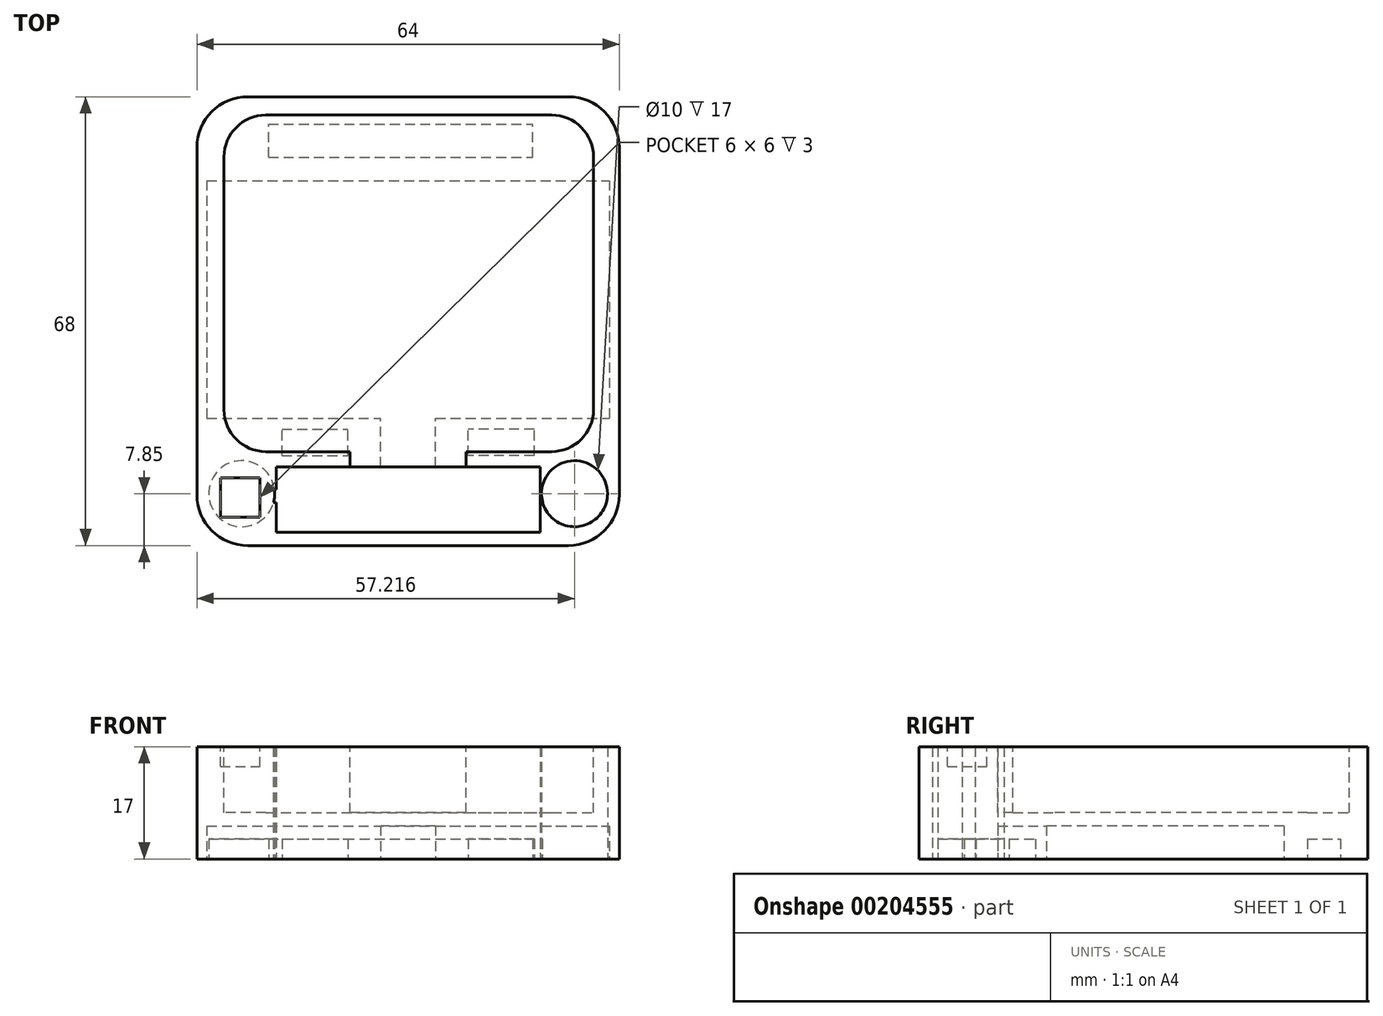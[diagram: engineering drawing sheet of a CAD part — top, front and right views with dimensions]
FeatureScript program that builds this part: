
annotation { "Feature Type Name" : "Feature", "Feature Type Description" : "" }
export const myFeature = defineFeature(function(context is Context, id is Id, definition is map)
    precondition{}
    {
        {
            var Q0;
            Q0=qCreatedBy(makeId("Top.planeOp"),FACE);
            var sketch = newSketch(context, id + "F0", { "sketchPlane" : qUnion([Q0])});
            skLineSegment(sketch, "E0.bottom", {"start": v(-24.3, 34) * mm, "end": v(24.3, 34) * mm});
            skLineSegment(sketch, "E0.top", {"start": v(-24.3, -34) * mm, "end": v(24.3, -34) * mm});
            skLineSegment(sketch, "E0.left", {"start": v(-32, 26.3) * mm, "end": v(-32, -26.3) * mm});
            skLineSegment(sketch, "E0.right", {"start": v(32, 26.3) * mm, "end": v(32, -26.3) * mm});
            skPoint(sketch, "E0.middle", {"position": v(0, 0) * mm});
            skPoint(sketch, "E1.visualSharp", {"position": v(32, 34) * mm});
            skArc(sketch, "E1.filletArc", {"start": v(32, 26.3) * mm, "mid": v(29.75, 31.75) * mm, "end": v(24.3, 34) * mm});
            skPoint(sketch, "E2.visualSharp", {"position": v(-32, 34) * mm});
            skArc(sketch, "E2.filletArc", {"start": v(-24.3, 34) * mm, "mid": v(-29.75, 31.75) * mm, "end": v(-32, 26.3) * mm});
            skPoint(sketch, "E3.visualSharp", {"position": v(-32, -34) * mm});
            skArc(sketch, "E3.filletArc", {"start": v(-32, -26.3) * mm, "mid": v(-29.75, -31.75) * mm, "end": v(-24.3, -34) * mm});
            skPoint(sketch, "E4.visualSharp", {"position": v(32, -34) * mm});
            skArc(sketch, "E4.filletArc", {"start": v(24.3, -34) * mm, "mid": v(29.75, -31.75) * mm, "end": v(32, -26.3) * mm});
            skLineSegment(sketch, "E5", {"start": v(0, -34) * mm, "end": v(0, -32) * mm});
            skPoint(sketch, "E5.endSnap0", {"position": v(0, -34) * mm});
            skLineSegment(sketch, "E6.bottom", {"start": v(0, -32) * mm, "end": v(-20, -32) * mm});
            skLineSegment(sketch, "E6.top", {"start": v(0, -22.07) * mm, "end": v(-20, -22.07) * mm});
            skLineSegment(sketch, "E6.left", {"start": v(0, -32) * mm, "end": v(0, -22.07) * mm});
            skLineSegment(sketch, "E6.right", {"start": v(-20, -32) * mm, "end": v(-20, -22.07) * mm});
            skLineSegment(sketch, "E7.bottom", {"start": v(0, -32) * mm, "end": v(20, -32) * mm});
            skLineSegment(sketch, "E7.top", {"start": v(0, -22.07) * mm, "end": v(20, -22.07) * mm});
            skLineSegment(sketch, "E7.right", {"start": v(20, -32) * mm, "end": v(20, -22.07) * mm});
            skCircle(sketch, "E8", {"center": v(-25.22, -26.15) * mm, "radius": 5 * mm});
            skCircle(sketch, "E9.MirrorC", {"center": v(25.22, -26.15) * mm, "radius": 5 * mm});
            skLineSegment(sketch, "E10.MirrorCS", {"start": v(30.68, -30.61) * mm, "end": v(28.93, -29.65) * mm});
            skLineSegment(sketch, "E11.bottom", {"start": v(-30.5, 21.3) * mm, "end": v(30.5, 21.3) * mm});
            skLineSegment(sketch, "E11.top", {"start": v(-30.5, -14.7) * mm, "end": v(30.5, -14.7) * mm});
            skLineSegment(sketch, "E11.left", {"start": v(-30.5, 21.3) * mm, "end": v(-30.5, -14.7) * mm});
            skLineSegment(sketch, "E11.right", {"start": v(30.5, 21.3) * mm, "end": v(30.5, -14.7) * mm});
            skLineSegment(sketch, "E12", {"start": v(-32, 15.13) * mm, "end": v(-30.5, 15.13) * mm});
            skLineSegment(sketch, "E13", {"start": v(30.5, 14.25) * mm, "end": v(32, 14.25) * mm});
            skLineSegment(sketch, "E14", {"start": v(-20.26, -25.53) * mm, "end": v(-20, -25.53) * mm});
            skLineSegment(sketch, "E15", {"start": v(-20, -25.53) * mm, "end": v(-20, -27.49) * mm});
            skLineSegment(sketch, "E16", {"start": v(-20, -27.49) * mm, "end": v(-20.4, -27.49) * mm});
            skLineSegment(sketch, "E17", {"start": v(20, -25.4) * mm, "end": v(20.27, -25.4) * mm});
            skLineSegment(sketch, "E18", {"start": v(20, -27.17) * mm, "end": v(20.32, -27.17) * mm});
            skLineSegment(sketch, "E19", {"start": v(-4.15, -22.07) * mm, "end": v(-4.15, -14.7) * mm});
            skLineSegment(sketch, "E20.MirrorCS", {"start": v(4.15, -22.07) * mm, "end": v(4.15, -14.7) * mm});
            skSolve(sketch);
        }
        {
            var Q0;
            Q0=makeQuery(id+"F0.imprint","IMPRINT",FACE,{"disambiguationData":[TD([[makeQuery(id+"F0.imprint","IMPRINT",EDGE,{"derivedFrom":sQuery(id+"F0.wireOp",EDGE,"E0.bottom")}),-1.0]])]});
            var Q1;
            {var subQ5=sQuery(id+"F0.wireOp",EDGE,"fJw1VMtN-DNDU-9MxT-oK31-EzQkojQoViIx.bottom");Q1=makeQuery(id+"F0.imprint","IMPRINT",FACE,{"disambiguationData":[TD([[makeQuery(id+"F0.imprint","IMPRINT",EDGE,{"derivedFrom":subQ5}),-1.0]])]});}
            var Q2;
            {var subQ14=sQuery(id+"F0.wireOp",EDGE,"E3.filletArc");Q2=makeQuery(id+"F0.imprint","IMPRINT",FACE,{"disambiguationData":[TD([[makeQuery(id+"F0.imprint","IMPRINT",EDGE,{"derivedFrom":subQ14}),1.0]])]});}
            var Q3;
            {var subQ0=sQuery(id+"F0.wireOp",EDGE,"E5");Q3=makeQuery(id+"F0.imprint","IMPRINT",FACE,{"disambiguationData":[TD([[makeQuery(id+"F0.imprint","IMPRINT",EDGE,{"derivedFrom":subQ0}),-1.0]])]});}
            var Q4;
            {var subQ0=sQuery(id+"F0.wireOp",EDGE,"fJw1VMtN-DNDU-9MxT-oK31-EzQkojQoViIx.left");var subQ1=sQuery(id+"F0.wireOp",EDGE,"E11.bottom");var subQ2=makeQuery(id+"F0.imprint","INTERSECT",VERTEX,{"derivedFrom":[subQ1,subQ0]});Q4=makeQuery(id+"F0.imprint","IMPRINT",FACE,{"disambiguationData":[TD([[makeQuery(id+"F0.imprint","IMPRINT",EDGE,{"disambiguationData":[TD([[subQ2,-1.0]])],"derivedFrom":subQ1}),-1.0]])]});}
            var Q5;
            {var subQ0=sQuery(id+"F0.wireOp",EDGE,"E11.left");var subQ6=sQuery(id+"F0.wireOp",EDGE,"E11.bottom");var subQ7=makeQuery(id+"F0.imprint","INTERSECT",VERTEX,{"derivedFrom":[subQ6,subQ0]});Q5=makeQuery(id+"F0.imprint","IMPRINT",FACE,{"disambiguationData":[TD([[makeQuery(id+"F0.imprint","IMPRINT",EDGE,{"disambiguationData":[TD([[subQ7,-1.0]])],"derivedFrom":subQ6}),-1.0]])]});}
            var Q6;
            {var subQ0=sQuery(id+"F0.wireOp",EDGE,"E11.right");var subQ4=sQuery(id+"F0.wireOp",EDGE,"E11.bottom");var subQ5=makeQuery(id+"F0.imprint","INTERSECT",VERTEX,{"derivedFrom":[subQ4,subQ0]});Q6=makeQuery(id+"F0.imprint","IMPRINT",FACE,{"disambiguationData":[TD([[makeQuery(id+"F0.imprint","IMPRINT",EDGE,{"disambiguationData":[TD([[subQ5,1.0]])],"derivedFrom":subQ4}),-1.0]])]});}
            var Q7;
            {var subQ5=sQuery(id+"F0.wireOp",EDGE,"fJw1VMtN-DNDU-9MxT-oK31-EzQkojQoViIx.top");Q7=makeQuery(id+"F0.imprint","IMPRINT",FACE,{"disambiguationData":[TD([[makeQuery(id+"F0.imprint","IMPRINT",EDGE,{"derivedFrom":subQ5}),1.0]])]});}
            var Q8;
            {var subQ0=sQuery(id+"F0.wireOp",EDGE,"E19");Q8=makeQuery(id+"F0.imprint","IMPRINT",FACE,{"disambiguationData":[TD([[makeQuery(id+"F0.imprint","IMPRINT",EDGE,{"derivedFrom":subQ0}),-1.0]])]});}
            extrude(context, id + "F1", {"entities" : qUnion([Q0, Q1, Q2, Q3, Q4, Q5, Q6, Q7, Q8]), "depth" : 17 * mm});
        }
        {
            var Q0;
            {var subQ0=sQuery(id+"F0.wireOp",EDGE,"fJw1VMtN-DNDU-9MxT-oK31-EzQkojQoViIx.left");var subQ1=sQuery(id+"F0.wireOp",EDGE,"E11.bottom");var subQ2=makeQuery(id+"F0.imprint","INTERSECT",VERTEX,{"derivedFrom":[subQ1,subQ0]});Q0=makeQuery(id+"F0.imprint","IMPRINT",FACE,{"disambiguationData":[TD([[makeQuery(id+"F0.imprint","IMPRINT",EDGE,{"disambiguationData":[TD([[subQ2,-1.0]])],"derivedFrom":subQ1}),-1.0]])]});}
            var Q1;
            {var subQ0=sQuery(id+"F0.wireOp",EDGE,"E19");Q1=makeQuery(id+"F0.imprint","IMPRINT",FACE,{"disambiguationData":[TD([[makeQuery(id+"F0.imprint","IMPRINT",EDGE,{"derivedFrom":subQ0}),-1.0]])]});}
            extrude(context, id + "F2", {"entities" : qUnion([Q0, Q1]), "operationType" : NewBodyOperationType.REMOVE, "depth" : 5 * mm});
        }
        {
            var Q0;
            Q0=makeQuery(id+"F0.imprint","IMPRINT",FACE,{"disambiguationData":[TD([[makeQuery(id+"F0.imprint","IMPRINT",EDGE,{"derivedFrom":sQuery(id+"F0.wireOp",EDGE,"E8")}),1.0]])]});
            var Q1;
            {var subQ0=sQuery(id+"F0.wireOp",EDGE,"E9.MirrorC");var subQ1=makeQuery(id+"F0.imprint","INTERSECT",VERTEX,{"derivedFrom":[subQ0,sQuery(id+"F0.wireOp",EDGE,"E10.MirrorCS")]});Q1=makeQuery(id+"F0.imprint","IMPRINT",FACE,{"disambiguationData":[TD([[makeQuery(id+"F0.imprint","IMPRINT",EDGE,{"disambiguationData":[TD([[subQ1,-1.0]])],"derivedFrom":subQ0}),-1.0]])]});}
            extrude(context, id + "F3", {"entities" : qUnion([Q0, Q1]), "operationType" : NewBodyOperationType.ADD, "depth" : 17 * mm});
        }
        {
            var Q0;
            {var subQ0=sQuery(id+"F0.wireOp",EDGE,"E9.MirrorC");var subQ1=makeQuery(id+"F0.imprint","INTERSECT",VERTEX,{"derivedFrom":[subQ0,sQuery(id+"F0.wireOp",EDGE,"E17")]});Q0=makeQuery(id+"F0.imprint","IMPRINT",FACE,{"disambiguationData":[TD([[makeQuery(id+"F0.imprint","IMPRINT",EDGE,{"disambiguationData":[TD([[subQ1,-1.0]])],"derivedFrom":subQ0}),-1.0]])]});}
            var Q1;
            {var subQ0=sQuery(id+"F0.wireOp",EDGE,"E8");var subQ1=makeQuery(id+"F0.imprint","INTERSECT",VERTEX,{"derivedFrom":[subQ0,sQuery(id+"F0.wireOp",EDGE,"E14")]});Q1=makeQuery(id+"F0.imprint","IMPRINT",FACE,{"disambiguationData":[TD([[makeQuery(id+"F0.imprint","IMPRINT",EDGE,{"disambiguationData":[TD([[subQ1,-1.0]])],"derivedFrom":subQ0}),1.0]])]});}
            extrude(context, id + "F4", {"entities" : qUnion([Q0, Q1]), "operationType" : NewBodyOperationType.REMOVE, "depth" : 3 * mm});
        }
        {
            var Q0;
            Q0=makeQuery(id+"F1.opExtrude","CAP_FACE",FACE,{"disambiguationData":[OSD([sQuery(id+"F0.wireOp",EDGE,"E0.bottom"),sQuery(id+"F0.wireOp",EDGE,"E0.top"),sQuery(id+"F0.wireOp",EDGE,"E0.left"),sQuery(id+"F0.wireOp",EDGE,"E0.right"),sQuery(id+"F0.wireOp",EDGE,"E1.filletArc"),sQuery(id+"F0.wireOp",EDGE,"E2.filletArc"),sQuery(id+"F0.wireOp",EDGE,"E3.filletArc"),sQuery(id+"F0.wireOp",EDGE,"E4.filletArc"),sQuery(id+"F0.wireOp",EDGE,"E6.bottom"),sQuery(id+"F0.wireOp",EDGE,"E6.top"),sQuery(id+"F0.wireOp",EDGE,"E6.right"),sQuery(id+"F0.wireOp",EDGE,"E7.bottom"),sQuery(id+"F0.wireOp",EDGE,"E7.top"),sQuery(id+"F0.wireOp",EDGE,"E7.right"),sQuery(id+"F0.wireOp",EDGE,"E8"),sQuery(id+"F0.wireOp",EDGE,"E9.MirrorC"),sQuery(id+"F0.wireOp",EDGE,"E14"),sQuery(id+"F0.wireOp",EDGE,"E16"),sQuery(id+"F0.wireOp",EDGE,"E17"),sQuery(id+"F0.wireOp",EDGE,"E18")])],"isStart":false});
            var sketch = newSketch(context, id + "F5", { "sketchPlane" : qUnion([Q0])});
            skLineSegment(sketch, "E21.bottom", {"start": v(-21.55, 31.23) * mm, "end": v(21.75, 31.23) * mm});
            skLineSegment(sketch, "E21.top", {"start": v(-21.55, -19.77) * mm, "end": v(21.75, -19.77) * mm});
            skLineSegment(sketch, "E21.left", {"start": v(-27.9, 24.88) * mm, "end": v(-27.9, -13.42) * mm});
            skLineSegment(sketch, "E21.right", {"start": v(28.1, 24.88) * mm, "end": v(28.1, -13.42) * mm});
            skPoint(sketch, "E22.visualSharp", {"position": v(-27.9, 31.23) * mm});
            skArc(sketch, "E22.filletArc", {"start": v(-21.55, 31.23) * mm, "mid": v(-26.04, 29.37) * mm, "end": v(-27.9, 24.88) * mm});
            skPoint(sketch, "E23.visualSharp", {"position": v(28.1, 31.23) * mm});
            skArc(sketch, "E23.filletArc", {"start": v(28.1, 24.88) * mm, "mid": v(26.24, 29.37) * mm, "end": v(21.75, 31.23) * mm});
            skPoint(sketch, "E24.visualSharp", {"position": v(28.1, -19.77) * mm});
            skArc(sketch, "E24.filletArc", {"start": v(21.75, -19.77) * mm, "mid": v(26.24, -17.91) * mm, "end": v(28.1, -13.42) * mm});
            skPoint(sketch, "E25.visualSharp", {"position": v(-27.9, -19.77) * mm});
            skArc(sketch, "E25.filletArc", {"start": v(-27.9, -13.42) * mm, "mid": v(-26.04, -17.91) * mm, "end": v(-21.55, -19.77) * mm});
            skLineSegment(sketch, "E26", {"start": v(8.8, -19.77) * mm, "end": v(8.8, -22.07) * mm});
            skLineSegment(sketch, "E27.MirrorCS", {"start": v(-8.8, -19.77) * mm, "end": v(-8.8, -22.07) * mm});
            skSolve(sketch);
        }
        {
            var Q0;
            Q0=makeQuery(id+"F5.imprint","IMPRINT",FACE,{"disambiguationData":[TD([[makeQuery(id+"F5.imprint","IMPRINT",EDGE,{"derivedFrom":sQuery(id+"F5.wireOp",EDGE,"E21.bottom")}),-1.0]])]});
            var Q1;
            {var subQ0=sQuery(id+"F5.wireOp",EDGE,"E26");Q1=makeQuery(id+"F5.imprint","IMPRINT",FACE,{"disambiguationData":[TD([[makeQuery(id+"F5.imprint","IMPRINT",EDGE,{"derivedFrom":subQ0}),-1.0]])]});}
            extrude(context, id + "F6", {"entities" : qUnion([Q0, Q1]), "operationType" : NewBodyOperationType.REMOVE, "oppositeDirection" : true, "depth" : 10 * mm});
        }
        {
            var Q0;
            Q0=makeQuery(id+"F0.imprint","IMPRINT",FACE,{"disambiguationData":[TD([[makeQuery(id+"F0.imprint","IMPRINT",EDGE,{"derivedFrom":sQuery(id+"F0.wireOp",EDGE,"E0.bottom")}),-1.0]])]});
            var sketch = newSketch(context, id + "F7", { "sketchPlane" : qUnion([Q0])});
            skLineSegment(sketch, "E28.bottom", {"start": v(-21.15, 24.85) * mm, "end": v(18.85, 24.85) * mm});
            skLineSegment(sketch, "E28.top", {"start": v(-21.15, 29.85) * mm, "end": v(18.85, 29.85) * mm});
            skLineSegment(sketch, "E28.left", {"start": v(-21.15, 24.85) * mm, "end": v(-21.15, 29.85) * mm});
            skLineSegment(sketch, "E28.right", {"start": v(18.85, 24.85) * mm, "end": v(18.85, 29.85) * mm});
            skLineSegment(sketch, "E29.bottom", {"start": v(-19.1, -20.38) * mm, "end": v(-9.1, -20.38) * mm});
            skLineSegment(sketch, "E29.top", {"start": v(-19.1, -16.38) * mm, "end": v(-9.1, -16.38) * mm});
            skLineSegment(sketch, "E29.left", {"start": v(-19.1, -20.38) * mm, "end": v(-19.1, -16.38) * mm});
            skLineSegment(sketch, "E29.right", {"start": v(-9.1, -20.38) * mm, "end": v(-9.1, -16.38) * mm});
            skLineSegment(sketch, "E30.MirrorCS", {"start": v(19.1, -20.38) * mm, "end": v(9.1, -20.38) * mm});
            skLineSegment(sketch, "E31.MirrorCS", {"start": v(19.1, -20.38) * mm, "end": v(19.1, -16.38) * mm});
            skLineSegment(sketch, "E32.MirrorCS", {"start": v(9.1, -20.38) * mm, "end": v(9.1, -16.38) * mm});
            skLineSegment(sketch, "E33.MirrorCS", {"start": v(19.1, -16.38) * mm, "end": v(9.1, -16.38) * mm});
            skSolve(sketch);
        }
        {
            var Q0;
            Q0=makeQuery(id+"F7.imprint","IMPRINT",FACE,{"disambiguationData":[TD([[makeQuery(id+"F7.imprint","IMPRINT",EDGE,{"derivedFrom":sQuery(id+"F7.wireOp",EDGE,"E29.bottom")}),1.0]])]});
            var Q1;
            Q1=makeQuery(id+"F7.imprint","IMPRINT",FACE,{"disambiguationData":[TD([[makeQuery(id+"F7.imprint","IMPRINT",EDGE,{"derivedFrom":sQuery(id+"F7.wireOp",EDGE,"E30.MirrorCS")}),-1.0]])]});
            var Q2;
            Q2=makeQuery(id+"F7.imprint","IMPRINT",FACE,{"disambiguationData":[TD([[makeQuery(id+"F7.imprint","IMPRINT",EDGE,{"derivedFrom":sQuery(id+"F7.wireOp",EDGE,"E28.bottom")}),1.0]])]});
            extrude(context, id + "F8", {"entities" : qUnion([Q0, Q1, Q2]), "operationType" : NewBodyOperationType.REMOVE, "depth" : 3 * mm});
        }
        {
            var Q0;
            Q0=makeQuery(id+"F5.imprint","IMPRINT",FACE,{"disambiguationData":[TD([[makeQuery(id+"F5.imprint","IMPRINT",EDGE,{"derivedFrom":sQuery(id+"F5.wireOp",EDGE,"E21.bottom")}),1.0]])]});
            var sketch = newSketch(context, id + "F9", { "sketchPlane" : qUnion([Q0])});
            skLineSegment(sketch, "E34.bottom", {"start": v(28.45, -29.72) * mm, "end": v(22.45, -29.72) * mm});
            skLineSegment(sketch, "E34.top", {"start": v(28.45, -23.72) * mm, "end": v(22.45, -23.72) * mm});
            skLineSegment(sketch, "E34.left", {"start": v(28.45, -29.72) * mm, "end": v(28.45, -23.72) * mm});
            skLineSegment(sketch, "E34.right", {"start": v(22.45, -29.72) * mm, "end": v(22.45, -23.72) * mm});
            skLineSegment(sketch, "E35.MirrorCS", {"start": v(-28.45, -29.72) * mm, "end": v(-22.45, -29.72) * mm});
            skLineSegment(sketch, "E36.MirrorCS", {"start": v(-28.45, -29.72) * mm, "end": v(-28.45, -23.72) * mm});
            skLineSegment(sketch, "E37.MirrorCS", {"start": v(-22.45, -29.72) * mm, "end": v(-22.45, -23.72) * mm});
            skLineSegment(sketch, "E38.MirrorCS", {"start": v(-28.45, -23.72) * mm, "end": v(-22.45, -23.72) * mm});
            skSolve(sketch);
        }
        {
            var Q0;
            Q0=makeQuery(id+"F9.imprint","IMPRINT",FACE,{"disambiguationData":[TD([[makeQuery(id+"F9.imprint","IMPRINT",EDGE,{"derivedFrom":sQuery(id+"F9.wireOp",EDGE,"E34.bottom")}),-1.0]])]});
            var Q1;
            Q1=makeQuery(id+"F9.imprint","IMPRINT",FACE,{"disambiguationData":[TD([[makeQuery(id+"F9.imprint","IMPRINT",EDGE,{"derivedFrom":sQuery(id+"F9.wireOp",EDGE,"E35.MirrorCS")}),1.0]])]});
            extrude(context, id + "F10", {"entities" : qUnion([Q0, Q1]), "operationType" : NewBodyOperationType.REMOVE, "oppositeDirection" : true, "depth" : 3 * mm});
        }
    });
